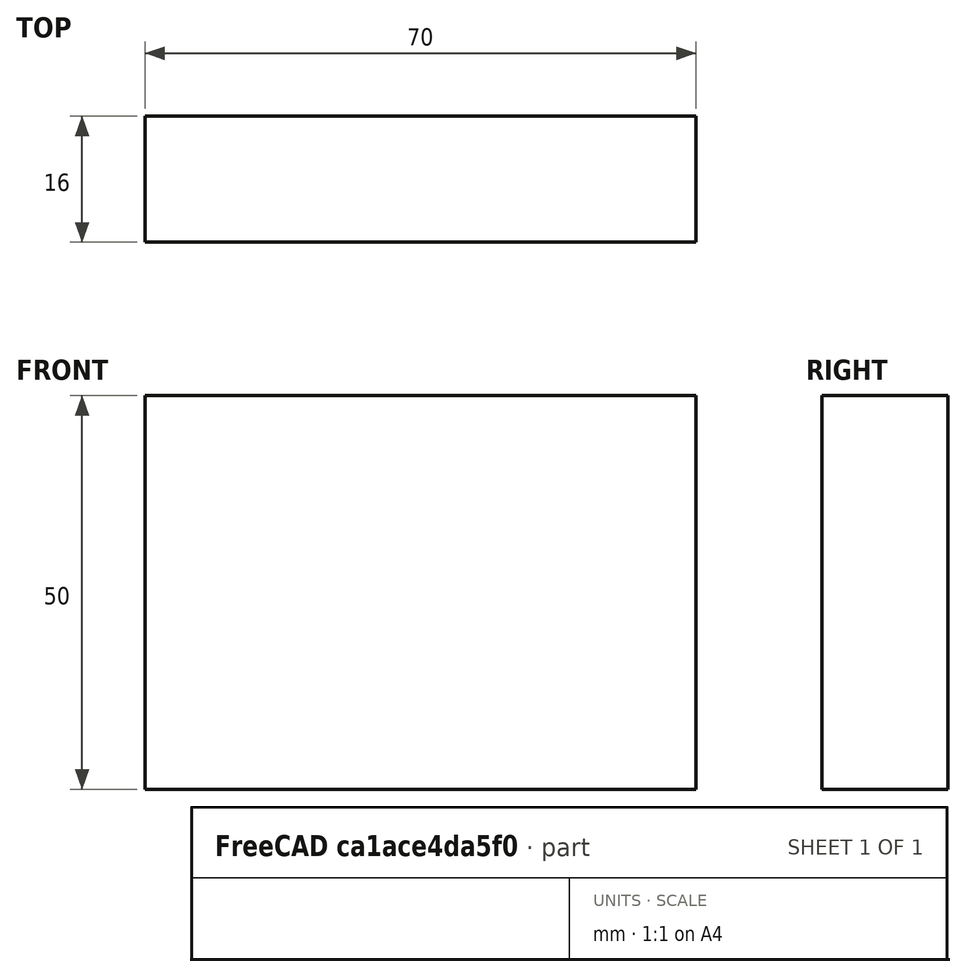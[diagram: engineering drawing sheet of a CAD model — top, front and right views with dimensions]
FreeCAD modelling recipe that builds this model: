
FCSTD DOCUMENT  (FreeCAD 0.15R4671 (Git))
Label: Flat Bar 70x16 EN10058 S235JR
License: All rights reserved
LicenseURL: http://en.wikipedia.org/wiki/All_rights_reserved
objects: Sketcher::SketchObject×1, Part::Extrusion×1
note: 2 computed .brp shape members not serialized (recipe doc carries the construction recipe); baked Part::Feature solids carry a one-line shape summary decoded from their .brp

FEATURE [Sketcher::SketchObject] Sketch
  sketch-geometry (4):
    g0: LineSegment StartX=-35 StartY=-8 StartZ=0 EndX=35 EndY=-8 EndZ=0
    g1: LineSegment StartX=35 StartY=-8 StartZ=0 EndX=35 EndY=8 EndZ=0
    g2: LineSegment StartX=35 StartY=8 StartZ=0 EndX=-35 EndY=8 EndZ=0
    g3: LineSegment StartX=-35 StartY=8 StartZ=0 EndX=-35 EndY=-8 EndZ=0
  constraints (12):
    c: Coincident(g0,g1)
    c: Coincident(g1,g2)
    c: Coincident(g2,g3)
    c: Coincident(g3,g0)
    c: Horizontal(g0)
    c: Horizontal(g2)
    c: Vertical(g1)
    c: Vertical(g3)
    c: Symmetric(g1,g2,g-2)
    c: Symmetric(g0,g1,g-1)
    c: DistanceY(g1) = 16
    c: DistanceX(g0) = 70
FEATURE [Part::Extrusion] Extrude  label="Flat Bar 70x16 EN10058 S235JR"
  Base = -> Sketch
  Dir = (0,0,50)
  Solid = true
